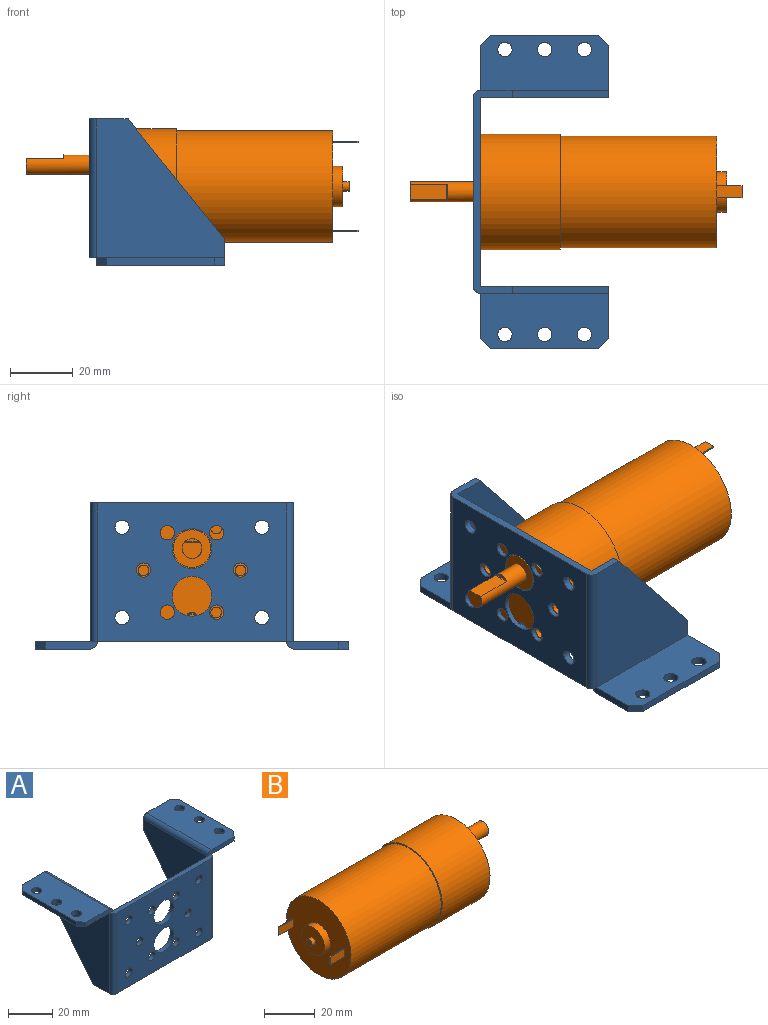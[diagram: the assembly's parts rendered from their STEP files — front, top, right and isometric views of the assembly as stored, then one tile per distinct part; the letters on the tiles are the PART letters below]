
ASSEMBLY  parts=2 mates=1
PART A: 48 faces, bbox 100.3x43.4x46.7 mm
  f0: plane 44.45x0.01mm, normal (-1,0,0), area 0.5mm2, adj f1,f2,f4,f19
  f1: plane 65.02x43.43mm, normal (0,0,1), area 146.9mm2, adj f0,f2,f3,f5,f18,f19,f20,f22
  f2: plane 60.45x44.45mm, normal (0,-1,0), area 2269.6mm2, adj f0,f1,f4,f5,f6,f7,f8,f9
  f3: plane 60.45x44.45mm, normal (0,1,0), area 2269.6mm2, adj f1,f4,f6,f7,f8,f9,f10,f11
  f4: plane 65.02x12.45mm, normal (0,0,-1), area 192.4mm2, adj f0,f2,f3,f5,f18,f19,f31,f32
  f5: plane 44.45x0.01mm, normal (1,0,0), area 0.5mm2, adj f1,f2,f4,f47
  f6: cylinder r=6.35mm len=12.7mm, axis (0,1,0), area 91.2mm2, adj f2,f3
  f7: cylinder r=6.35mm len=12.7mm, axis (0,1,0), area 91.2mm2, adj f2,f3
  f8: cylinder r=2.29mm len=4.57mm, axis (0,1,0), area 32.8mm2, adj f2,f3
  f9: cylinder r=2.29mm len=4.57mm, axis (0,1,0), area 32.8mm2, adj f2,f3
  f10: cylinder r=2.29mm len=4.57mm, axis (0,1,0), area 32.8mm2, adj f2,f3
  f11: cylinder r=2.29mm len=4.57mm, axis (0,1,0), area 32.8mm2, adj f2,f3
  f12: cylinder r=2.29mm len=4.57mm, axis (0,1,0), area 32.8mm2, adj f2,f3
  f13: cylinder r=2.29mm len=4.57mm, axis (0,1,0), area 32.8mm2, adj f2,f3
  f14: cylinder r=2.29mm len=4.57mm, axis (0,1,0), area 32.8mm2, adj f2,f3
  f15: cylinder r=2.29mm len=4.57mm, axis (0,1,0), area 32.8mm2, adj f2,f3
  f16: cylinder r=2.29mm len=4.57mm, axis (0,1,0), area 32.8mm2, adj f2,f3
  f17: cylinder r=2.29mm len=4.57mm, axis (0,1,0), area 32.8mm2, adj f2,f3
  f18: plane 44.45x41.15mm, normal (1,0,0), area 1230.4mm2, adj f1,f3,f4,f22,f31
  f19: cylinder r=2.54mm len=44.45mm, axis (0,0,-1), area 155.3mm2, adj f0,f1,f4,f32
  f20: plane 16.75x2.29mm, normal (0,-1,0), area 37mm2, adj f1,f21,f23,f24,f27
  f21: plane 41.15x17.64mm, normal (0,0,-1), area 666.2mm2, adj f20,f22,f25,f26,f27,f28,f29,f30
  f22: plane 16.76x8.1mm, normal (0,1,0), area 50.3mm2, adj f1,f18,f21,f23,f24,f25,f31,f32
  f23: cylinder r=2.54mm len=41.15mm, axis (0,1,0), area 143.8mm2, adj f1,f20,f22,f24
  f24: plane 41.15x17.64mm, normal (0,0,1), area 666.2mm2, adj f20,f22,f23,f25,f26,f27,f28,f29
  f25: plane 3.3x3.16mm, normal (-0.72,0.69,0), area 10.5mm2, adj f21,f22,f24,f26
  f26: plane 34.54x2.29mm, normal (-1,0,0), area 79mm2, adj f21,f24,f25,f27
  f27: plane 3.3x3.16mm, normal (-0.72,-0.69,0), area 10.5mm2, adj f20,f21,f24,f26
  f28: cylinder r=2.29mm len=4.57mm, axis (0,0,1), area 32.8mm2, adj f21,f24
  f29: cylinder r=2.29mm len=4.57mm, axis (0,0,1), area 32.8mm2, adj f21,f24
  f30: cylinder r=2.29mm len=4.57mm, axis (0,0,1), area 32.8mm2, adj f21,f24
  f31: plane 38.64x30.99mm, normal (0,0.78,-0.63), area 113.2mm2, adj f4,f18,f22,f32
  f32: plane 44.45x41.15mm, normal (-1,0,0), area 1230.4mm2, adj f4,f19,f21,f22,f31
  f33: plane 41.15x17.64mm, normal (0,0,1), area 666.2mm2, adj f35,f36,f37,f38,f39,f40,f41,f42
  f34: plane 41.15x17.64mm, normal (0,0,-1), area 666.2mm2, adj f35,f36,f37,f38,f39,f40,f41,f42
  f35: plane 16.75x2.29mm, normal (0,-1,0), area 37mm2, adj f1,f33,f34,f36,f46
  f36: plane 3.3x3.16mm, normal (0.72,-0.69,0), area 10.5mm2, adj f33,f34,f35,f37
  f37: plane 34.54x2.29mm, normal (1,0,0), area 79mm2, adj f33,f34,f36,f38
  f38: plane 3.3x3.16mm, normal (0.72,0.69,0), area 10.5mm2, adj f33,f34,f37,f39
  f39: plane 16.76x8.1mm, normal (0,1,0), area 50.3mm2, adj f1,f33,f34,f38,f43,f44,f45,f46
  f40: cylinder r=2.29mm len=4.57mm, axis (0,0,1), area 32.8mm2, adj f33,f34
  f41: cylinder r=2.29mm len=4.57mm, axis (0,0,1), area 32.8mm2, adj f33,f34
  f42: cylinder r=2.29mm len=4.57mm, axis (0,0,1), area 32.8mm2, adj f33,f34
  f43: plane 38.64x30.99mm, normal (0,0.78,-0.63), area 113.2mm2, adj f4,f39,f44,f45
  f44: plane 44.45x41.15mm, normal (1,0,0), area 1230.4mm2, adj f4,f34,f39,f43,f47
  f45: plane 44.45x41.15mm, normal (-1,0,0), area 1230.4mm2, adj f1,f3,f4,f39,f43
  f46: cylinder r=2.54mm len=41.15mm, axis (0,-1,0), area 143.8mm2, adj f1,f33,f35,f39
  f47: cylinder r=2.54mm len=44.45mm, axis (0,0,1), area 155.3mm2, adj f1,f4,f5,f44
PART B: 70 faces, bbox 106.2x37x37 mm
  f0: torus R=1.65mm, axis (1,0,0), area 2.2mm2, adj f5,f45
  f1: torus R=1.65mm, axis (1,0,0), area 2.2mm2, adj f3,f47
  f2: torus R=1.65mm, axis (1,0,0), area 2.2mm2, adj f4,f46
  f3: cylinder r=1.78mm len=3.56mm, axis (-1,0,0), area 24.1mm2, adj f1,f19
  f4: cylinder r=1.78mm len=3.56mm, axis (-1,0,0), area 24.1mm2, adj f2,f20
  f5: cylinder r=1.78mm len=3.56mm, axis (-1,0,0), area 24.1mm2, adj f0,f21
  f6: cylinder r=1.91mm len=3.81mm, axis (1,0,0), area 30.4mm2, adj f20,f25
  f7: cylinder r=1.91mm len=3.81mm, axis (1,0,0), area 30.4mm2, adj f21,f25
  f8: cylinder r=1.91mm len=3.81mm, axis (1,0,0), area 30.4mm2, adj f19,f25
  f9: cylinder r=1.57mm len=3.15mm, axis (1,0,0), area 21.1mm2, adj f23,f32
  f10: cylinder r=6.45mm len=12.9mm, axis (1,0,0), area 128.7mm2, adj f22,f23
  f11: cylinder r=1.73mm len=3.5mm, axis (1,0,0), area 38mm2, adj f25,f31
  f12: cylinder r=1.73mm len=3.5mm, axis (1,0,0), area 38mm2, adj f25,f30
  f13: cylinder r=1.73mm len=3.5mm, axis (1,0,0), area 38mm2, adj f25,f29
  f14: cylinder r=1.73mm len=3.5mm, axis (1,0,0), area 38mm2, adj f25,f28
  f15: cylinder r=3.17mm len=20.2mm, axis (-1,0,0), area 334.8mm2, adj f24,f27,f43,f44,f69
  f16: cylinder r=6mm len=12mm, axis (-1,0,0), area 50.9mm2, adj f24,f25
  f17: cylinder r=18.5mm len=37mm, axis (-1,0,0), area 3080.9mm2, adj f25,f26
  f18: cylinder r=17.9mm len=50mm, axis (1,0,0), area 5623.5mm2, adj f22,f26
  f19: plane 3.81x3.81mm, normal (1,0,0), area 1.5mm2, adj f3,f8
  f20: plane 3.81x3.81mm, normal (1,0,0), area 1.5mm2, adj f4,f6
  f21: plane 3.81x3.81mm, normal (1,0,0), area 1.5mm2, adj f5,f7
  f22: plane 35.8x35.8mm, normal (-1,0,0), area 872.1mm2, adj f10,f18,f33,f34,f35,f36,f38,f39
  f23: plane 12.9x12.9mm, normal (-1,0,0), area 123mm2, adj f9,f10
  f24: plane 12x12mm, normal (1,0,0), area 81.4mm2, adj f15,f16
  f25: plane 37x37mm, normal (1,0,0), area 890.4mm2, adj f6,f7,f8,f11,f12,f13,f14,f16
  f26: plane 37x37mm, normal (-1,0,0), area 68.6mm2, adj f17,f18
  f27: plane 4.51x0.94mm, normal (1,0,0), area 2.9mm2, adj f15,f69
  f28: plane 3.45x3.45mm, normal (1,0,0), area 9.4mm2, adj f14
  f29: plane 3.45x3.45mm, normal (1,0,0), area 9.4mm2, adj f13
  f30: plane 3.45x3.45mm, normal (1,0,0), area 9.4mm2, adj f12
  f31: plane 3.45x3.45mm, normal (1,0,0), area 9.4mm2, adj f11
  f32: plane 3.15x3.15mm, normal (-1,0,0), area 7.8mm2, adj f9
  f33: plane 8.13x0.48mm, normal (0,0,1), area 3.9mm2, adj f22,f34,f36,f37
  f34: plane 8.13x3.86mm, normal (0,1,0), area 31.4mm2, adj f22,f33,f35,f37
  f35: plane 8.13x0.48mm, normal (0,0,-1), area 3.9mm2, adj f22,f34,f36,f37
  f36: plane 8.13x3.86mm, normal (0,-1,0), area 31.4mm2, adj f22,f33,f35,f37
  f37: plane 3.86x0.48mm, normal (-1,0,0), area 1.9mm2, adj f33,f34,f35,f36
  f38: plane 8.13x0.48mm, normal (0,0,1), area 3.9mm2, adj f22,f39,f41,f42
  f39: plane 8.13x3.86mm, normal (0,1,0), area 31.4mm2, adj f22,f38,f40,f42
  f40: plane 8.13x0.48mm, normal (0,0,-1), area 3.9mm2, adj f22,f39,f41,f42
  f41: plane 8.13x3.86mm, normal (0,-1,0), area 31.4mm2, adj f22,f38,f40,f42
  f42: plane 3.86x0.48mm, normal (-1,0,0), area 1.9mm2, adj f38,f39,f40,f41
  f43: plane 11.75x4.96mm, normal (0,1,0), area 58.3mm2, adj f15,f44,f69
  f44: plane 6.35x5.16mm, normal (1,0,0), area 27.5mm2, adj f15,f43
  f45: plane 3.3x3.3mm, normal (1,0,0), area 3.7mm2, adj f0,f48,f49,f50,f51,f52,f53
  f46: plane 3.3x3.3mm, normal (1,0,0), area 3.7mm2, adj f2,f55,f56,f57,f58,f59,f60
  f47: plane 3.3x3.3mm, normal (1,0,0), area 3.7mm2, adj f1,f62,f63,f64,f65,f66,f67
  f48: plane 1.38x1.27mm, normal (0,1,0), area 1.7mm2, adj f45,f49,f53,f54
  f49: plane 1.27x1.19mm, normal (0,0.5,-0.87), area 1.7mm2, adj f45,f48,f50,f54
  f50: plane 1.27x1.19mm, normal (0,-0.5,-0.87), area 1.7mm2, adj f45,f49,f51,f54
  f51: plane 1.38x1.27mm, normal (0,-1,0), area 1.7mm2, adj f45,f50,f52,f54
  f52: plane 1.27x1.19mm, normal (0,-0.5,0.87), area 1.7mm2, adj f45,f51,f53,f54
  f53: plane 1.27x1.19mm, normal (0,0.5,0.87), area 1.7mm2, adj f45,f48,f52,f54
  f54: plane 2.75x2.38mm, normal (1,0,0), area 4.9mm2, adj f48,f49,f50,f51,f52,f53
  f55: plane 1.27x1.19mm, normal (0,0.5,-0.87), area 1.7mm2, adj f46,f56,f60,f61
  f56: plane 1.27x1.19mm, normal (0,-0.5,-0.87), area 1.7mm2, adj f46,f55,f57,f61
  f57: plane 1.38x1.27mm, normal (0,-1,0), area 1.7mm2, adj f46,f56,f58,f61
  f58: plane 1.27x1.19mm, normal (0,-0.5,0.87), area 1.7mm2, adj f46,f57,f59,f61
  f59: plane 1.27x1.19mm, normal (0,0.5,0.87), area 1.7mm2, adj f46,f58,f60,f61
  f60: plane 1.38x1.27mm, normal (0,1,0), area 1.7mm2, adj f46,f55,f59,f61
  f61: plane 2.75x2.38mm, normal (1,0,0), area 4.9mm2, adj f55,f56,f57,f58,f59,f60
  f62: plane 1.38x1.27mm, normal (0,1,0), area 1.7mm2, adj f47,f63,f67,f68
  f63: plane 1.27x1.19mm, normal (0,0.5,-0.87), area 1.7mm2, adj f47,f62,f64,f68
  f64: plane 1.27x1.19mm, normal (0,-0.5,-0.87), area 1.7mm2, adj f47,f63,f65,f68
  f65: plane 1.38x1.27mm, normal (0,-1,0), area 1.7mm2, adj f47,f64,f66,f68
  f66: plane 1.27x1.19mm, normal (0,-0.5,0.87), area 1.7mm2, adj f47,f65,f67,f68
  f67: plane 1.27x1.19mm, normal (0,0.5,0.87), area 1.7mm2, adj f47,f62,f66,f68
  f68: plane 2.75x2.38mm, normal (1,0,0), area 4.9mm2, adj f62,f63,f64,f65,f66,f67
  f69: cylinder r=0.25mm len=4.96mm, axis (0,0,1), area 1.9mm2, adj f15,f27,f43
PLACE A rot(axis=(0.71,0.71,0),180deg) t=(0,-30.23,44.45)mm
PLACE B rot(axis=(0,-0.71,-0.71),180deg) t=(27.85,0,22.84)mm
MATE fastened A.f6 <-> B.f15  axis (-1,0,0) through (0,0,29.85)mm
